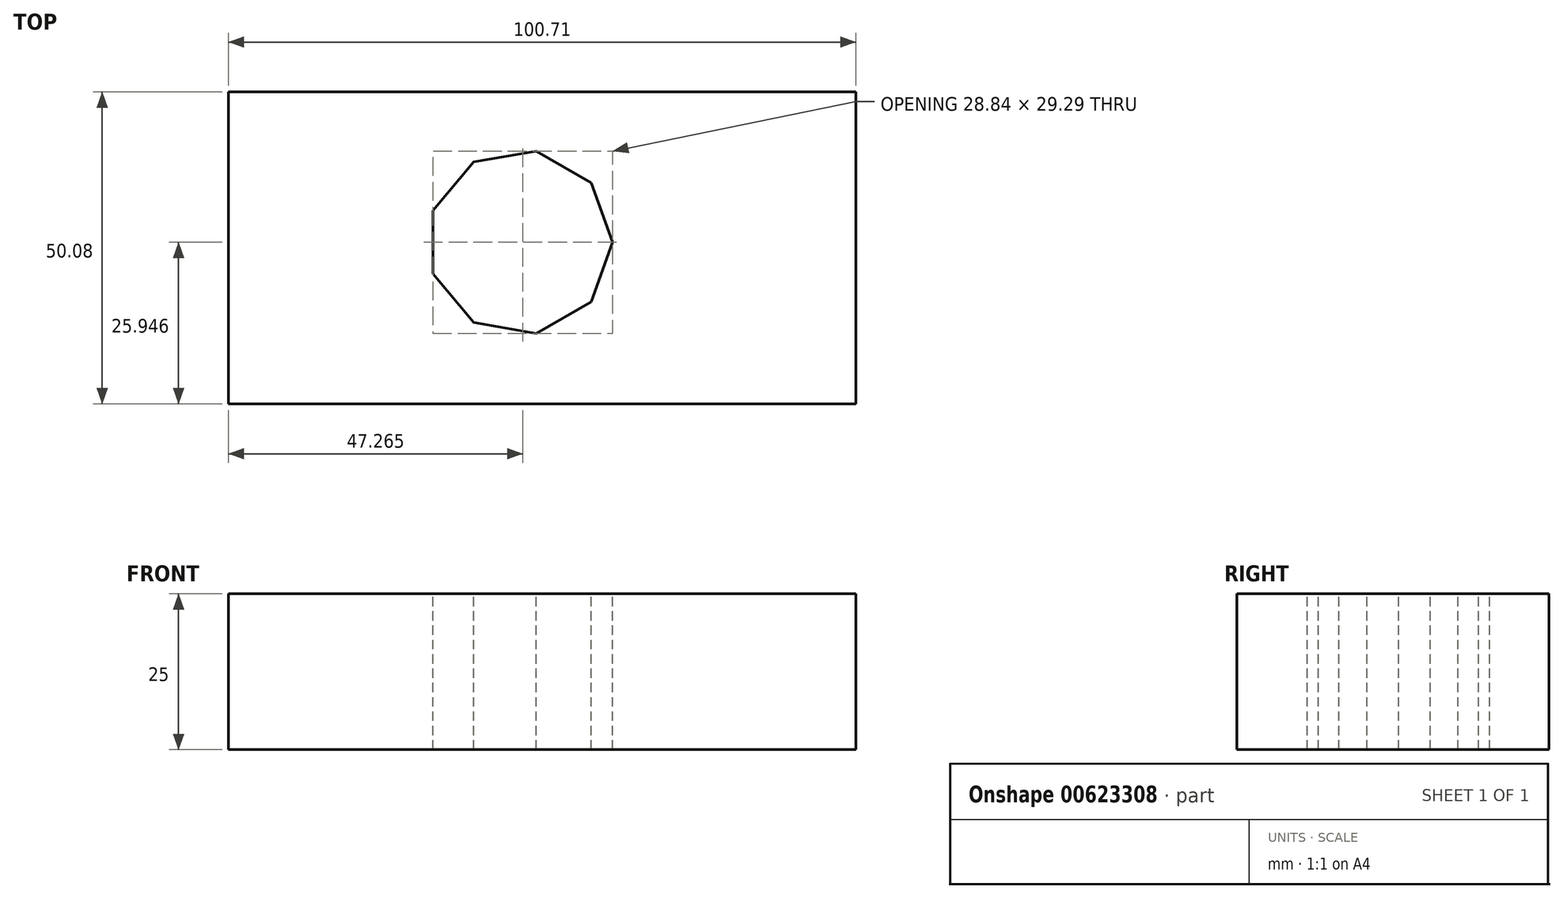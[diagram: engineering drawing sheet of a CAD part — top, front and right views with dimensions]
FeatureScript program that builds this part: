
annotation { "Feature Type Name" : "Feature", "Feature Type Description" : "" }
export const myFeature = defineFeature(function(context is Context, id is Id, definition is map)
    precondition{}
    {
        {
            var Q0;
            Q0=qCreatedBy(makeId("Top.planeOp"),FACE);
            var sketch = newSketch(context, id + "F0", { "sketchPlane" : qUnion([Q0])});
            skLineSegment(sketch, "E0.bottom", {"start": v(-64.69, 41.1) * mm, "end": v(36.02, 41.1) * mm});
            skLineSegment(sketch, "E0.top", {"start": v(-64.69, -8.98) * mm, "end": v(36.02, -8.98) * mm});
            skLineSegment(sketch, "E0.left", {"start": v(-64.69, 41.1) * mm, "end": v(-64.69, -8.98) * mm});
            skLineSegment(sketch, "E0.right", {"start": v(36.02, 41.1) * mm, "end": v(36.02, -8.98) * mm});
            skSolve(sketch);
        }
        {
            var Q0;
            Q0=makeQuery(id+"F0.imprint","IMPRINT",FACE,{"disambiguationData":[TD([[makeQuery(id+"F0.imprint","IMPRINT",EDGE,{"derivedFrom":sQuery(id+"F0.wireOp",EDGE,"E0.bottom")}),-1.0]])]});
            extrude(context, id + "F1", {"entities" : qUnion([Q0]), "depth" : 25 * mm, "offsetDistance" : 25 * mm});
        }
        {
            var Q0;
            Q0=makeQuery(id+"F1.opExtrude","CAP_FACE",FACE,{"disambiguationData":[OSD([sQuery(id+"F0.wireOp",EDGE,"E0.bottom"),sQuery(id+"F0.wireOp",EDGE,"E0.top"),sQuery(id+"F0.wireOp",EDGE,"E0.left"),sQuery(id+"F0.wireOp",EDGE,"E0.right")])],"isStart":false});
            var sketch = newSketch(context, id + "F2", { "sketchPlane" : qUnion([Q0])});
            skCircle(sketch, "E1.cCircle", {"center": v(-17.87, 16.97) * mm, "radius": 13.97 * mm, "construction": true});
            skLineSegment(sketch, "E1.0", {"start": v(-31.84, 11.88) * mm, "end": v(-31.84, 22.05) * mm});
            skLineSegment(sketch, "E1.1", {"start": v(-31.84, 22.05) * mm, "end": v(-25.3, 29.84) * mm});
            skLineSegment(sketch, "E1.2", {"start": v(-25.3, 29.84) * mm, "end": v(-15.3, 31.6) * mm});
            skLineSegment(sketch, "E1.3", {"start": v(-15.3, 31.6) * mm, "end": v(-6.48, 26.52) * mm});
            skLineSegment(sketch, "E1.4", {"start": v(-6.48, 26.52) * mm, "end": v(-3, 16.97) * mm});
            skLineSegment(sketch, "E1.5", {"start": v(-3, 16.97) * mm, "end": v(-6.48, 7.4) * mm});
            skLineSegment(sketch, "E1.6", {"start": v(-6.48, 7.4) * mm, "end": v(-15.3, 2.32) * mm});
            skLineSegment(sketch, "E1.7", {"start": v(-15.3, 2.32) * mm, "end": v(-25.3, 4.09) * mm});
            skLineSegment(sketch, "E1.8", {"start": v(-25.3, 4.09) * mm, "end": v(-31.84, 11.88) * mm});
            skPoint(sketch, "E1.0.midPoint", {"position": v(-31.84, 16.97) * mm});
            skSolve(sketch);
        }
        {
            var Q0;
            Q0=makeQuery(id+"F2.imprint","IMPRINT",FACE,{"disambiguationData":[TD([[makeQuery(id+"F2.imprint","IMPRINT",EDGE,{"derivedFrom":sQuery(id+"F2.wireOp",EDGE,"E1.0")}),-1.0]])]});
            extrude(context, id + "F3", {"entities" : qUnion([Q0]), "operationType" : NewBodyOperationType.REMOVE, "oppositeDirection" : true, "depth" : 25 * mm, "offsetDistance" : 25 * mm});
        }
    });
